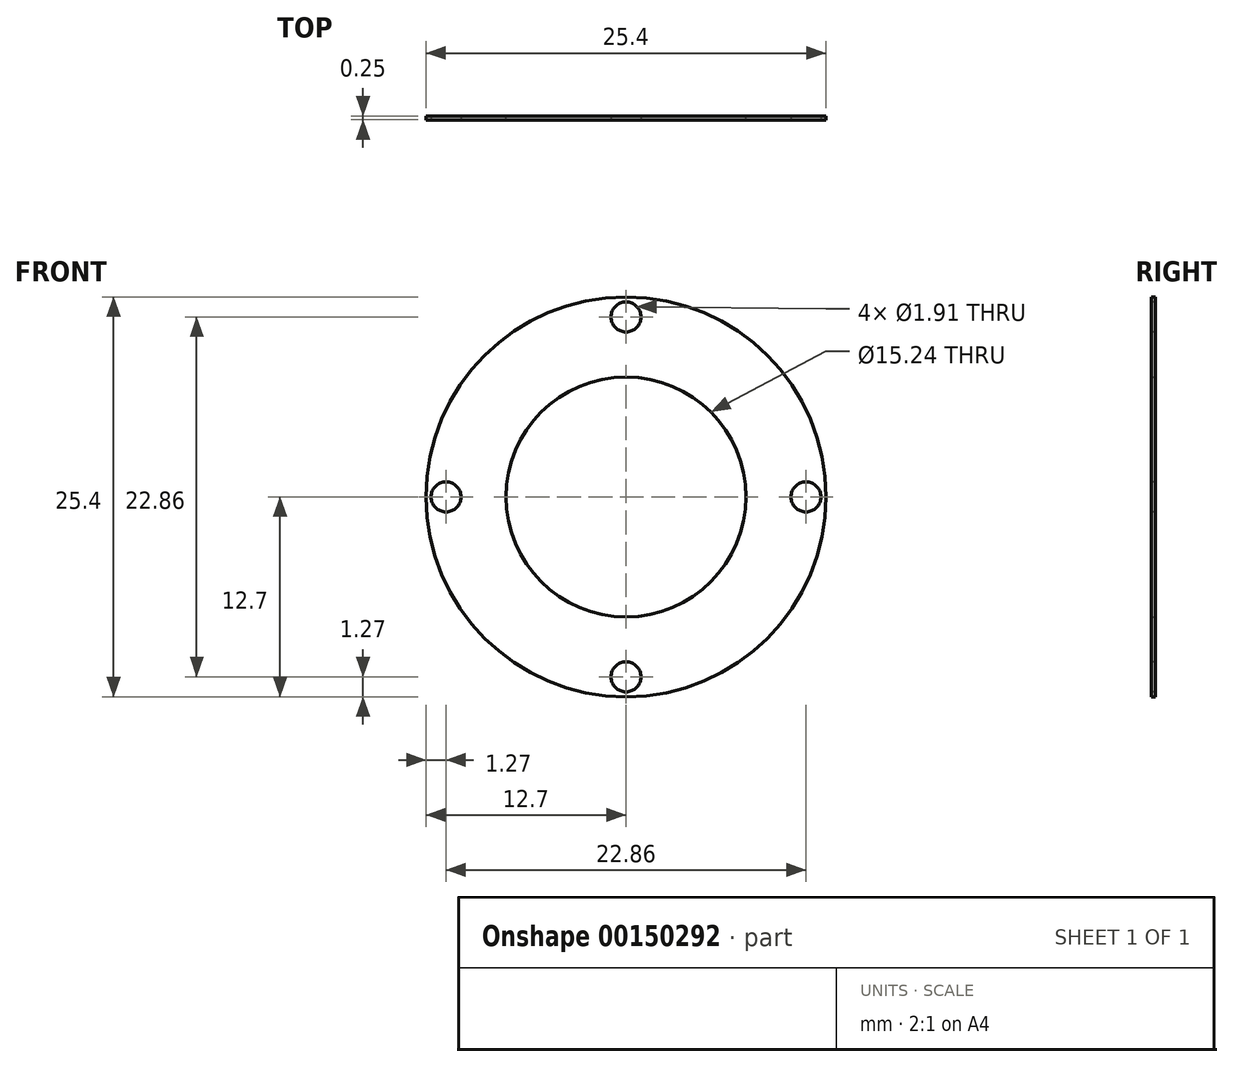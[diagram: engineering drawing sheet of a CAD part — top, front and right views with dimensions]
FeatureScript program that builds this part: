
annotation { "Feature Type Name" : "Feature", "Feature Type Description" : "" }
export const myFeature = defineFeature(function(context is Context, id is Id, definition is map)
    precondition{}
    {
        {
            var Q0;
            Q0=qCreatedBy(makeId("Front.planeOp"),FACE);
            var sketch = newSketch(context, id + "F0", { "sketchPlane" : qUnion([Q0])});
            skCircle(sketch, "E0", {"center": v(0, 0) * mm, "radius": 12.7 * mm});
            skCircle(sketch, "E1", {"center": v(0, 0) * mm, "radius": 7.62 * mm});
            skSolve(sketch);
        }
        {
            var Q0;
            Q0 = qSketchRegion(id + "F0", true);
            extrude(context, id + "F1", {"entities" : qUnion([Q0]), "depth" : 0.25 * mm});
        }
        {
            var Q0;
            Q0=makeQuery(id+"F1.opExtrude","CAP_FACE",FACE,{"disambiguationData":[OSD([sQuery(id+"F0.wireOp",EDGE,"E0"),sQuery(id+"F0.wireOp",EDGE,"E1")])],"isStart":false});
            var sketch = newSketch(context, id + "F2", { "sketchPlane" : qUnion([Q0])});
            skCircle(sketch, "E2", {"center": v(0, 11.43) * mm, "radius": 0.95 * mm});
            skCircle(sketch, "E3", {"center": v(11.43, 0) * mm, "radius": 0.95 * mm});
            skCircle(sketch, "E4", {"center": v(0, -11.43) * mm, "radius": 0.95 * mm});
            skCircle(sketch, "E5", {"center": v(-11.43, 0) * mm, "radius": 0.95 * mm});
            skSolve(sketch);
        }
        {
            var Q0;
            Q0 = qSketchRegion(id + "F2", true);
            extrude(context, id + "F3", {"entities" : qUnion([Q0]), "operationType" : NewBodyOperationType.REMOVE, "oppositeDirection" : true, "depth" : 25.4 * mm});
        }
    });
